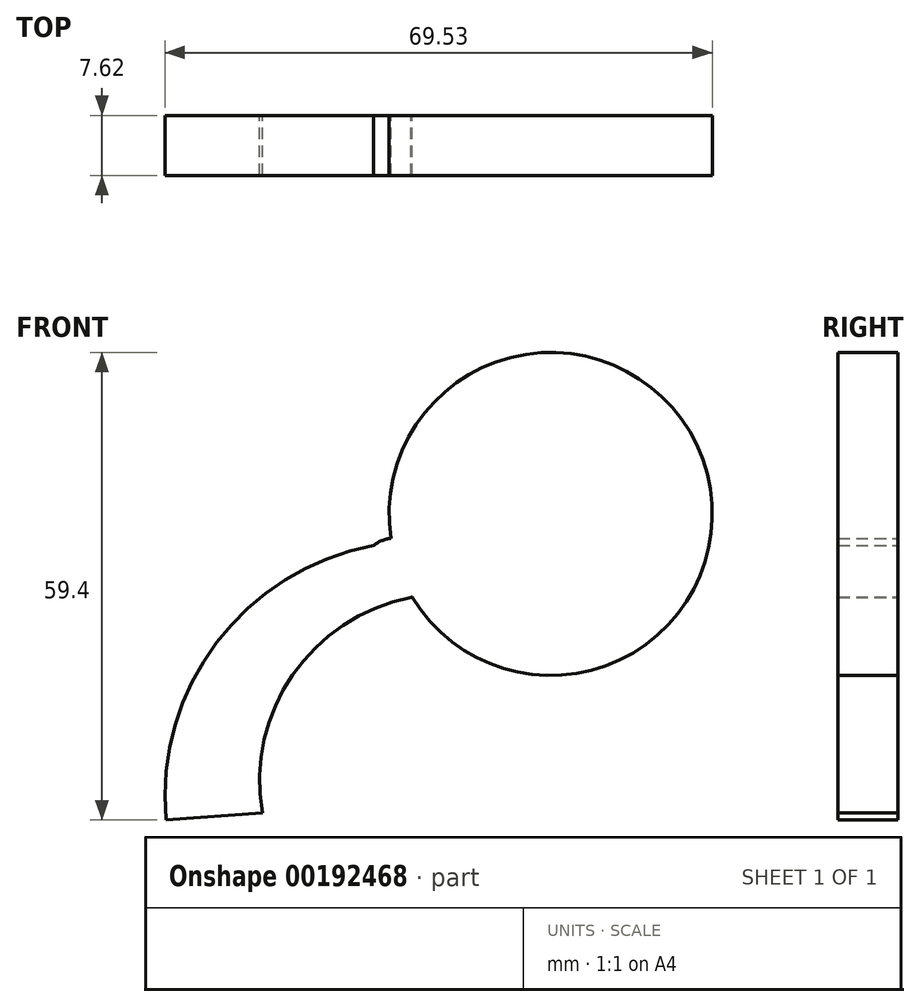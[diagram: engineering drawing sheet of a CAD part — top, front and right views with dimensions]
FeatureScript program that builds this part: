
annotation { "Feature Type Name" : "Feature", "Feature Type Description" : "" }
export const myFeature = defineFeature(function(context is Context, id is Id, definition is map)
    precondition{}
    {
        {
            var Q0;
            Q0=qCreatedBy(makeId("Front.planeOp"),FACE);
            var sketch = newSketch(context, id + "F0", { "sketchPlane" : qUnion([Q0])});
            skCircle(sketch, "E0", {"center": v(0.9, 4) * mm, "radius": 20.52 * mm});
            skPoint(sketch, "E0.first.point", {"position": v(0, 24.5) * mm});
            skPoint(sketch, "E0.second.point", {"position": v(0, -16.5) * mm});
            skPoint(sketch, "E0.third.point", {"position": v(-14.6, -9.42) * mm});
            skArc(sketch, "E1", {"start": v(-19.22, 0) * mm, "mid": v(-45.2, -11.5) * mm, "end": v(-51.84, -39.11) * mm});
            skArc(sketch, "E2", {"start": v(50.42, -39.11) * mm, "mid": v(45.7, -12.06) * mm, "end": v(21.03, 0) * mm});
            skSolve(sketch);
        }
        {
            var Q0;
            {var subQ0=sQuery(id+"F0.wireOp",EDGE,"E0");var subQ1=makeQuery(id+"F0.imprint","IMPRINT",VERTEX,{"disambiguationData":[OD(0.0)],"derivedFrom":subQ0});Q0=makeQuery(id+"F0.imprint","IMPRINT",FACE,{"disambiguationData":[TD([[makeQuery(id+"F0.imprint","IMPRINT",EDGE,{"disambiguationData":[TD([[subQ1,-1.0]])],"derivedFrom":subQ0}),1.0]])]});}
            extrude(context, id + "F1", {"entities" : qUnion([Q0]), "depth" : 7.62 * mm});
        }
        {
            var Q0;
            Q0=qCreatedBy(makeId("Front.planeOp"),FACE);
            var sketch = newSketch(context, id + "F2", { "sketchPlane" : qUnion([Q0])});
            skArc(sketch, "E3", {"start": v(-21.58, 0) * mm, "mid": v(-41.52, -12.34) * mm, "end": v(-47.97, -34.88) * mm});
            skArc(sketch, "E4", {"start": v(-16.87, -6.6) * mm, "mid": v(-31.88, -16.42) * mm, "end": v(-35.72, -33.94) * mm});
            skLineSegment(sketch, "E5", {"start": v(-47.97, -34.88) * mm, "end": v(-35.72, -33.94) * mm});
            skArc(sketch, "E6", {"start": v(-16.87, -6.6) * mm, "mid": v(-15.7, -0.78) * mm, "end": v(-21.58, 0) * mm});
            skArc(sketch, "E7", {"start": v(49.1, -31.58) * mm, "mid": v(42.46, -8.76) * mm, "end": v(20.36, 0) * mm});
            skArc(sketch, "E8", {"start": v(42.5, -31.58) * mm, "mid": v(35.28, -14.3) * mm, "end": v(18, -7.08) * mm});
            skLineSegment(sketch, "E9", {"start": v(42.5, -31.58) * mm, "end": v(49.1, -31.58) * mm});
            skSolve(sketch);
        }
        {
            var Q0;
            Q0=makeQuery(id+"F2.imprint","IMPRINT",FACE,{"disambiguationData":[TD([[makeQuery(id+"F2.imprint","IMPRINT",EDGE,{"derivedFrom":sQuery(id+"F2.wireOp",EDGE,"E3")}),1.0]])]});
            extrude(context, id + "F3", {"entities" : qUnion([Q0]), "operationType" : NewBodyOperationType.ADD, "depth" : 7.62 * mm});
        }
    });
